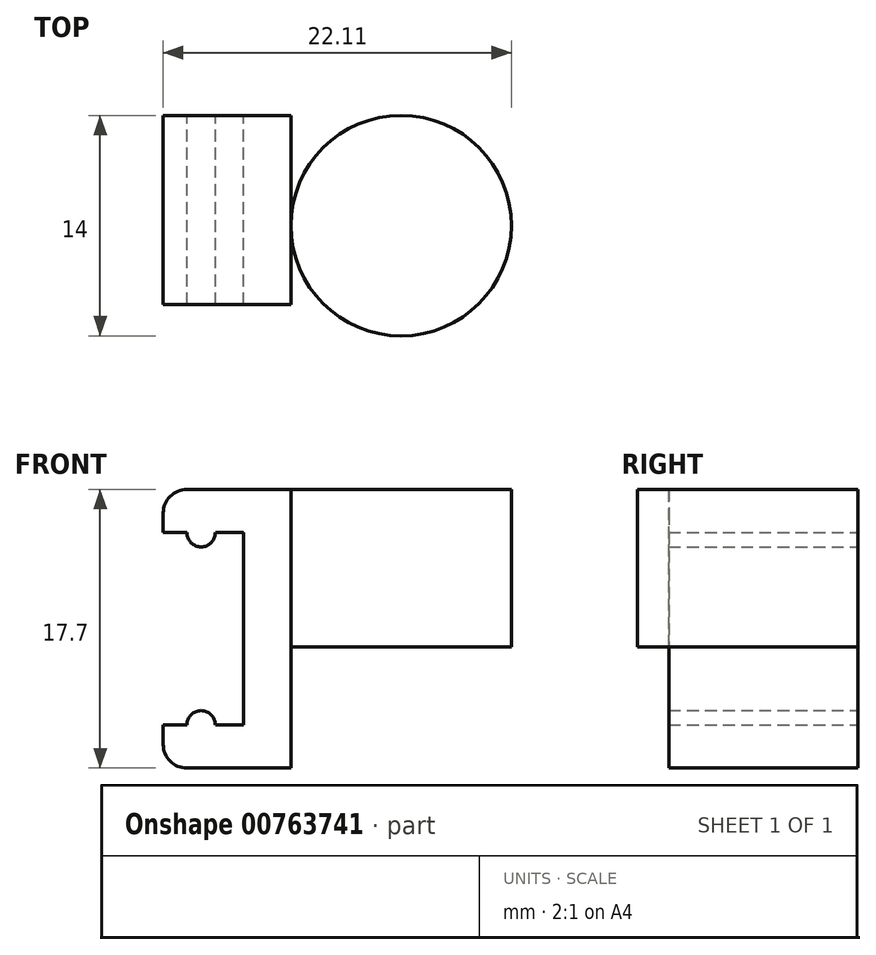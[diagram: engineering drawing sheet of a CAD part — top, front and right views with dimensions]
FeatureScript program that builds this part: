
annotation { "Feature Type Name" : "Feature", "Feature Type Description" : "" }
export const myFeature = defineFeature(function(context is Context, id is Id, definition is map)
    precondition{}
    {
        {
            var Q0;
            Q0=qCreatedBy(makeId("Front.planeOp"),FACE);
            var sketch = newSketch(context, id + "F0", { "sketchPlane" : qUnion([Q0])});
            skLineSegment(sketch, "E0", {"start": v(1.5, -0.54) * mm, "end": v(8.11, -0.54) * mm});
            skLineSegment(sketch, "E1", {"start": v(8.11, -0.54) * mm, "end": v(8.11, 17.16) * mm});
            skLineSegment(sketch, "E2", {"start": v(8.11, 17.16) * mm, "end": v(1.5, 17.16) * mm});
            skLineSegment(sketch, "E3", {"start": v(0, 17.7) * mm, "end": v(0, 14.4) * mm});
            skLineSegment(sketch, "E4", {"start": v(0, 14.4) * mm, "end": v(1.51, 14.4) * mm});
            skLineSegment(sketch, "E5", {"start": v(5.11, 14.4) * mm, "end": v(5.11, 2.2) * mm});
            skLineSegment(sketch, "E6", {"start": v(5.1, 2.2) * mm, "end": v(3.31, 2.2) * mm});
            skLineSegment(sketch, "E7", {"start": v(0, 2.2) * mm, "end": v(0, 0) * mm});
            skLineSegment(sketch, "E8", {"start": v(0, 15.66) * mm, "end": v(0, 0.96) * mm, "construction": true});
            skArc(sketch, "E9", {"start": v(1.51, 14.4) * mm, "mid": v(2.41, 13.5) * mm, "end": v(3.31, 14.4) * mm});
            skLineSegment(sketch, "E10", {"start": v(-1.44, 8.3) * mm, "end": v(25.11, 8.3) * mm, "construction": true});
            skPoint(sketch, "E10.startSnap0", {"position": v(5.11, 8.3) * mm});
            skArc(sketch, "E11.MirrorC", {"start": v(1.51, 2.2) * mm, "mid": v(2.41, 3.1) * mm, "end": v(3.31, 2.2) * mm});
            skLineSegment(sketch, "E12.trimOffspring", {"start": v(3.31, 14.4) * mm, "end": v(5.11, 14.4) * mm});
            skLineSegment(sketch, "E13.trimOffspring", {"start": v(1.51, 2.2) * mm, "end": v(0, 2.2) * mm});
            skPoint(sketch, "E14.visualSharp", {"position": v(8.11, 17.16) * mm});
            skLineSegment(sketch, "E14.filletArc", {"start": v(8.11, 17.16) * mm, "end": v(8.11, 17.16) * mm});
            skPoint(sketch, "E15.visualSharp", {"position": v(8.11, -0.54) * mm});
            skLineSegment(sketch, "E15.filletArc", {"start": v(8.11, -0.54) * mm, "end": v(8.11, -0.54) * mm});
            skArc(sketch, "E16.filletArc", {"start": v(0, 0.96) * mm, "mid": v(0.44, -0.1) * mm, "end": v(1.5, -0.54) * mm});
            skPoint(sketch, "E17.newPointA", {"position": v(0, 17.16) * mm});
            skArc(sketch, "E17.filletArc", {"start": v(1.5, 17.16) * mm, "mid": v(0.44, 16.72) * mm, "end": v(0, 15.66) * mm});
            skSolve(sketch);
        }
        {
            var Q0;
            Q0=makeQuery(id+"F0.imprint","IMPRINT",FACE,{"disambiguationData":[TD([[makeQuery(id+"F0.imprint","IMPRINT",EDGE,{"derivedFrom":sQuery(id+"F0.wireOp",EDGE,"E0")}),1.0]])]});
            extrude(context, id + "F1", {"entities" : qUnion([Q0]), "depth" : 12 * mm, "offsetDistance" : 25 * mm});
        }
        {
            var Q0;
            Q0=makeQuery(id+"F1.opExtrude","SWEPT_FACE",FACE,{"disambiguationData":[OSD([sQuery(id+"F0.wireOp",EDGE,"E2")])]});
            var sketch = newSketch(context, id + "F2", { "sketchPlane" : qUnion([Q0])});
            skCircle(sketch, "E18", {"center": v(15.11, -7) * mm, "radius": 7 * mm});
            skSolve(sketch);
        }
        {
            var Q0;
            Q0 = qSketchRegion(id + "F2", true);
            extrude(context, id + "F3", {"entities" : qUnion([Q0]), "oppositeDirection" : true, "depth" : 10 * mm, "offsetDistance" : 25 * mm});
        }
    });
